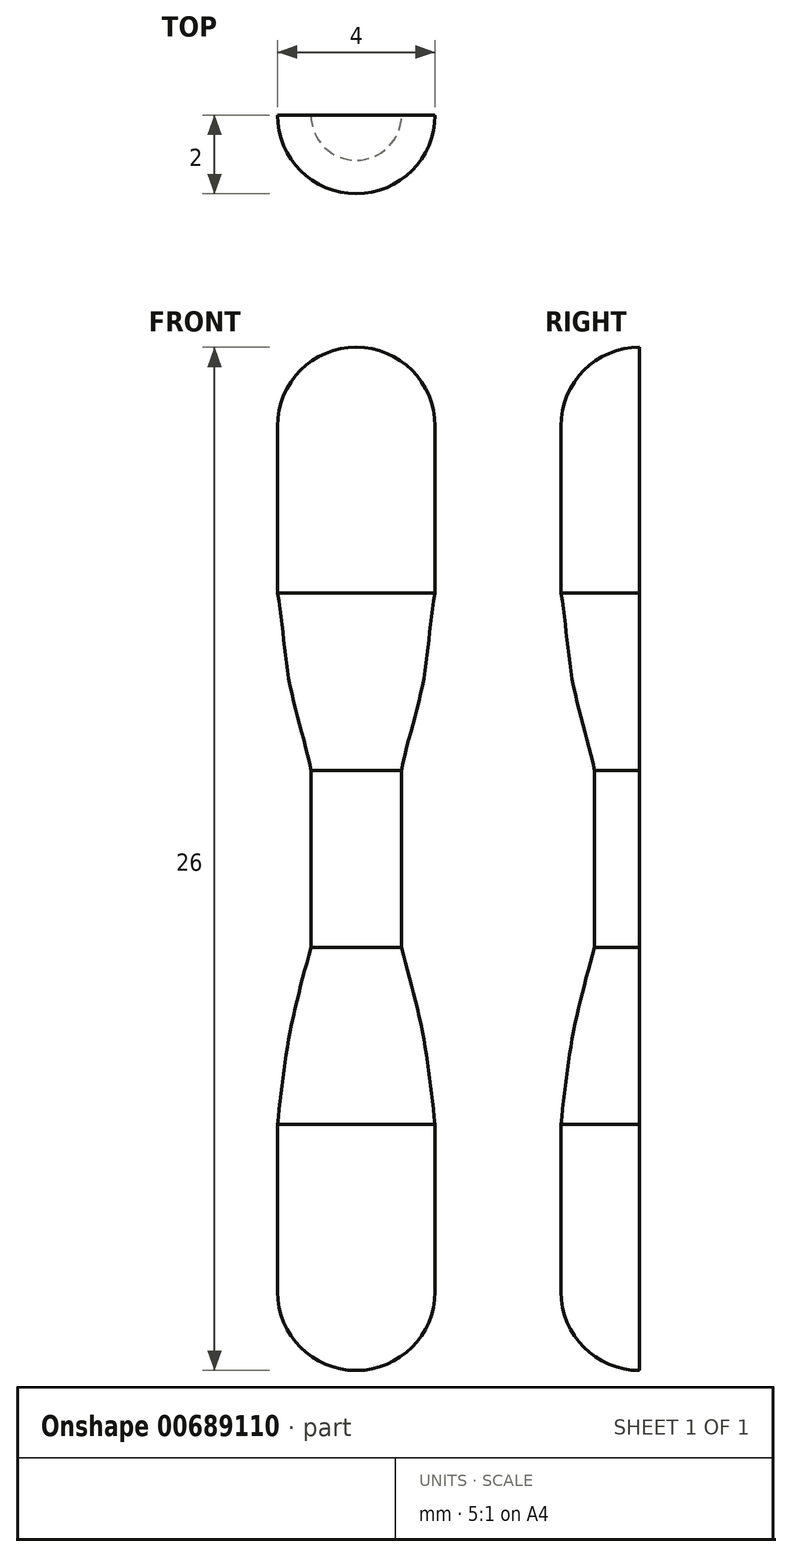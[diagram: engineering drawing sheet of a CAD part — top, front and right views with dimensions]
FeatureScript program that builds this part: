
annotation { "Feature Type Name" : "Feature", "Feature Type Description" : "" }
export const myFeature = defineFeature(function(context is Context, id is Id, definition is map)
    precondition{}
    {
        {
            var Q0;
            Q0=qCreatedBy(makeId("Front.planeOp"),FACE);
            var sketch = newSketch(context, id + "F0", { "sketchPlane" : qUnion([Q0])});
            skLineSegment(sketch, "E0", {"start": v(0, 0) * mm, "end": v(0, 26) * mm});
            skLineSegment(sketch, "E1", {"start": v(0, 13) * mm, "end": v(0, 15.25) * mm});
            skLineSegment(sketch, "E2", {"start": v(0, 13) * mm, "end": v(0, 10.75) * mm});
            skLineSegment(sketch, "E3", {"start": v(1.15, 10.75) * mm, "end": v(1.15, 13) * mm});
            skLineSegment(sketch, "E4", {"start": v(1.15, 13) * mm, "end": v(1.15, 15.25) * mm});
            skLineSegment(sketch, "E5", {"start": v(0, 13) * mm, "end": v(0, 19.75) * mm});
            skLineSegment(sketch, "E6", {"start": v(0, 13) * mm, "end": v(0, 6.25) * mm});
            skFitSpline(sketch, "E7", {"points": [v(1.15, 15.25) * mm, v(1.7, 17.5) * mm, v(2, 19.75) * mm], "startDerivative": vector(0.86, 4.43) * mm, "endDerivative": vector(0.84, 4.57) * mm});
            skLineSegment(sketch, "E8", {"start": v(0, 17.5) * mm, "end": v(0, 19.75) * mm});
            skLineSegment(sketch, "E9", {"start": v(0, 6.25) * mm, "end": v(0, 8.5) * mm});
            skFitSpline(sketch, "E10", {"points": [v(1.15, 10.75) * mm, v(1.7, 8.5) * mm, v(2, 6.25) * mm], "startDerivative": vector(1.22, -4.47) * mm, "endDerivative": vector(0.48, -4.53) * mm});
            skLineSegment(sketch, "E11", {"start": v(0, 26) * mm, "end": v(0, 24) * mm});
            skArc(sketch, "E12", {"start": v(2, 24) * mm, "mid": v(1.41, 25.41) * mm, "end": v(0, 26) * mm});
            skLineSegment(sketch, "E13", {"start": v(2, 19.75) * mm, "end": v(2, 24) * mm});
            skArc(sketch, "E14", {"start": v(0, 0) * mm, "mid": v(1.41, 0.59) * mm, "end": v(2, 2) * mm});
            skLineSegment(sketch, "E15", {"start": v(2, 2) * mm, "end": v(2, 6.25) * mm});
            skLineSegment(sketch, "E16", {"start": v(0, 26) * mm, "end": v(0, 0) * mm});
            skSolve(sketch);
        }
        {
            var Q0;
            Q0=makeQuery(id+"F0.imprint","IMPRINT",FACE,{"disambiguationData":[TD([[makeQuery(id+"F0.imprint","IMPRINT",EDGE,{"derivedFrom":sQuery(id+"F0.wireOp",EDGE,"E3")}),1.0]])]});
            var Q1;
            Q1=sQuery(id+"F0.wireOp",EDGE,"E16");
            revolve(context, id + "F1", {"entities" : qUnion([Q0]), "axis" : qUnion([Q1]), "revolveType" : RevolveType.ONE_DIRECTION, "angle" : 180 * degree});
        }
    });
